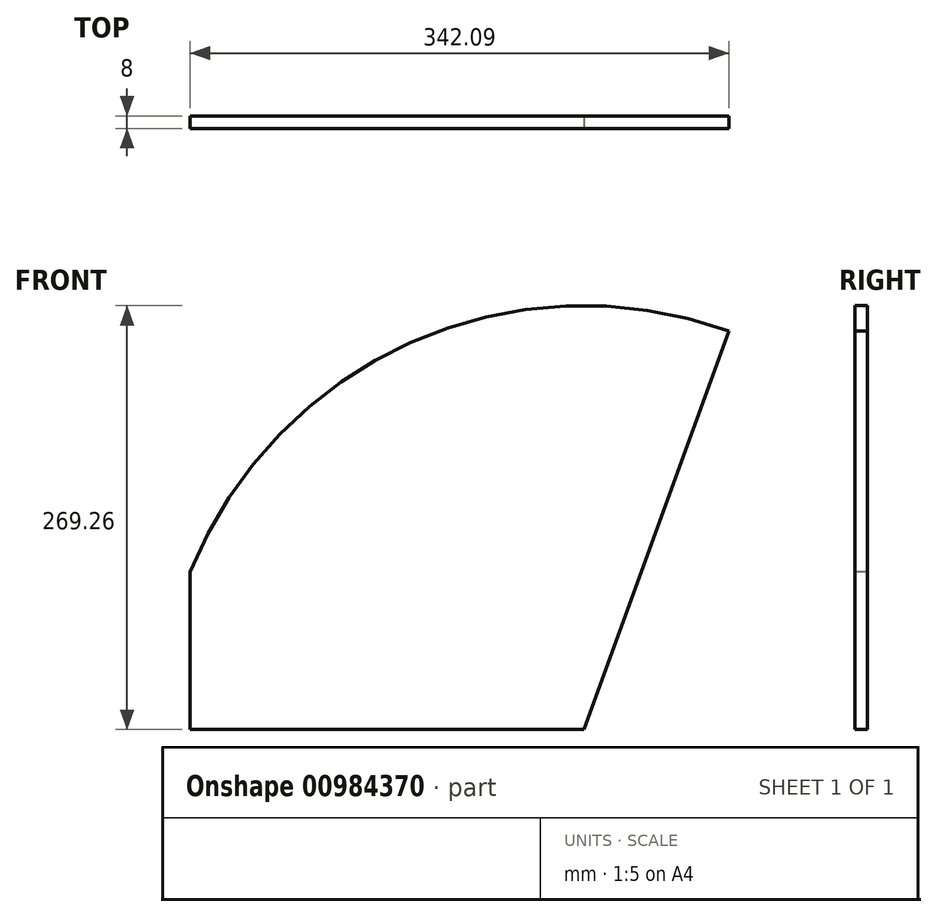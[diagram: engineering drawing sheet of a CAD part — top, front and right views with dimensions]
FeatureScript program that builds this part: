
annotation { "Feature Type Name" : "Feature", "Feature Type Description" : "" }
export const myFeature = defineFeature(function(context is Context, id is Id, definition is map)
    precondition{}
    {
        {
            var Q0;
            Q0=qCreatedBy(makeId("Front.planeOp"),FACE);
            var sketch = newSketch(context, id + "F0", { "sketchPlane" : qUnion([Q0])});
            skLineSegment(sketch, "E0", {"start": v(0, 0) * mm, "end": v(250, 0) * mm});
            skLineSegment(sketch, "E1", {"start": v(0, 0) * mm, "end": v(0, 100) * mm});
            skLineSegment(sketch, "E2", {"start": v(250, 0) * mm, "end": v(342.1, 253.02) * mm});
            skArc(sketch, "E3", {"start": v(0, 100) * mm, "mid": v(140.06, 245.79) * mm, "end": v(342.1, 253.02) * mm});
            skSolve(sketch);
        }
        {
            var Q0;
            Q0=qSketchRegion(id+"F0",true);
            extrude(context, id + "F1", {"entities" : qUnion([Q0]), "oppositeDirection" : true, "depth" : 8 * mm, "offsetDistance" : 25 * mm});
        }
    });
